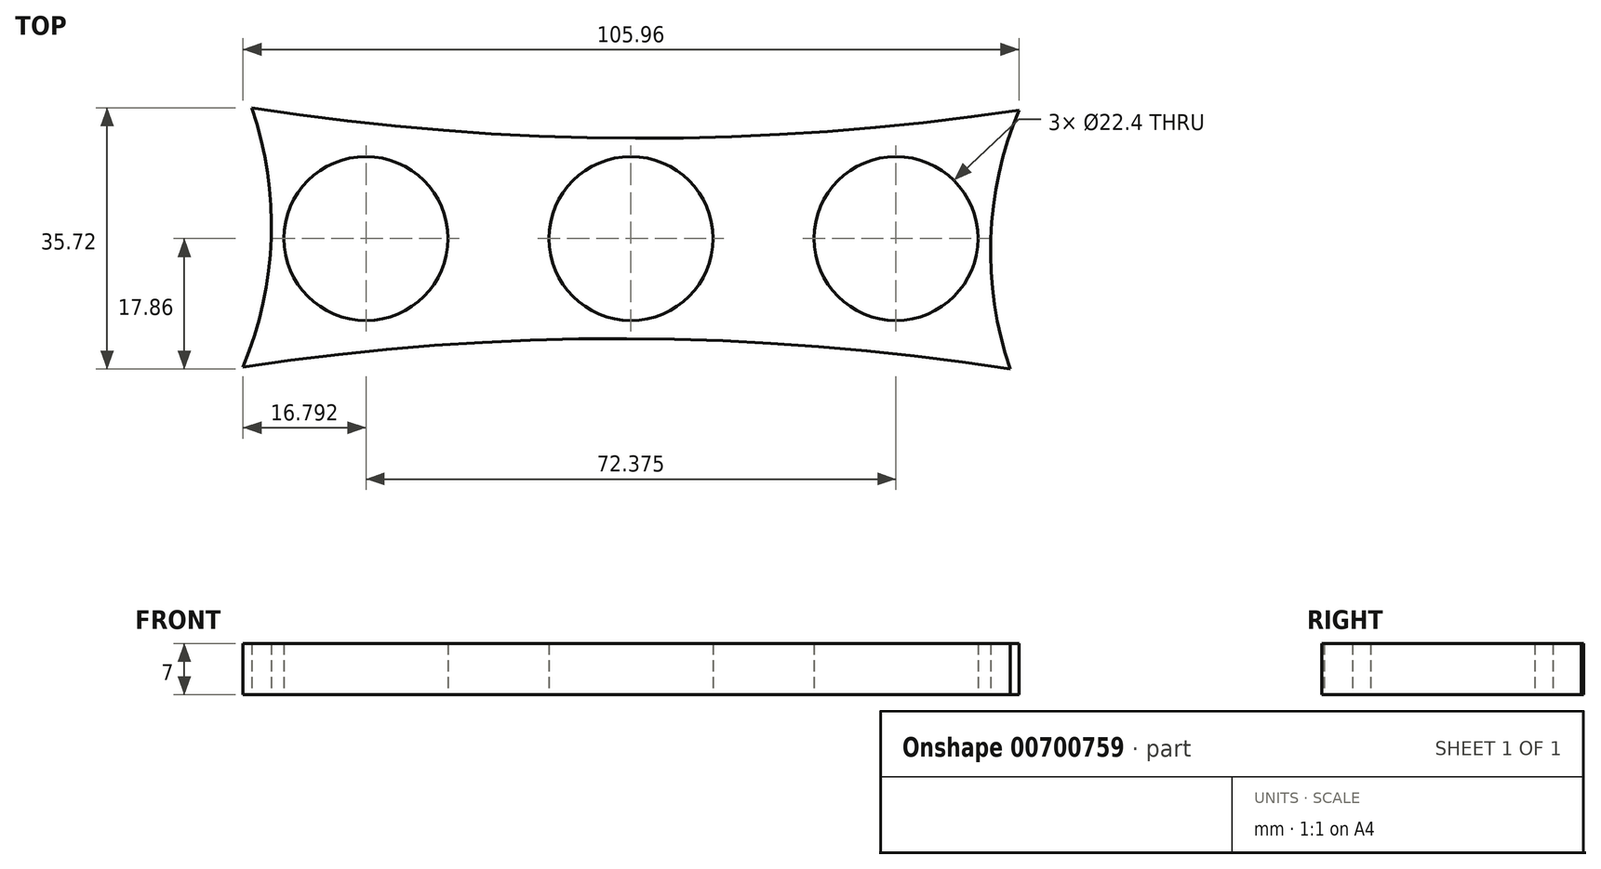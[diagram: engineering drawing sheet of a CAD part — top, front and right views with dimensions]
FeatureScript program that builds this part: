
annotation { "Feature Type Name" : "Feature", "Feature Type Description" : "" }
export const myFeature = defineFeature(function(context is Context, id is Id, definition is map)
    precondition{}
    {
        {
            var Q0;
            Q0=qCreatedBy(makeId("Top.planeOp"),FACE);
            var sketch = newSketch(context, id + "F0", { "sketchPlane" : qUnion([Q0])});
            skCircle(sketch, "E0", {"center": v(0, 0) * mm, "radius": 11.2 * mm});
            skCircle(sketch, "E1", {"center": v(-36.19, 0) * mm, "radius": 11.2 * mm});
            skArc(sketch, "E2", {"start": v(-49.1, 2.71) * mm, "mid": v(-49.38, 0.37) * mm, "end": v(-49.24, -1.98) * mm});
            skArc(sketch, "E3.1.0", {"start": v(49.1, -2.71) * mm, "mid": v(49.38, -0.37) * mm, "end": v(49.24, 1.98) * mm});
            skCircle(sketch, "E3.1.1", {"center": v(36.19, 0) * mm, "radius": 11.2 * mm});
            skArc(sketch, "E4", {"start": v(-49.37, -0.6) * mm, "mid": v(-49.26, 0.82) * mm, "end": v(-49.2, 2.24) * mm});
            skArc(sketch, "E5", {"start": v(-52.98, -17.56) * mm, "mid": v(-49.13, 0.04) * mm, "end": v(-51.76, 17.86) * mm});
            skArc(sketch, "E6.1.0", {"start": v(52.98, 17.56) * mm, "mid": v(49.13, -0.04) * mm, "end": v(51.76, -17.86) * mm});
            skArc(sketch, "E7", {"start": v(-51.76, 17.86) * mm, "mid": v(0.6, 13.7) * mm, "end": v(52.98, 17.56) * mm});
            skArc(sketch, "E8.1.0", {"start": v(51.76, -17.86) * mm, "mid": v(-0.6, -13.7) * mm, "end": v(-52.98, -17.56) * mm});
            skSolve(sketch);
        }
        {
            var Q0;
            Q0=makeQuery(id+"F0.imprint","IMPRINT",FACE,{"disambiguationData":[TD([[makeQuery(id+"F0.imprint","IMPRINT",EDGE,{"derivedFrom":sQuery(id+"F0.wireOp",EDGE,"E0")}),-1.0]])]});
            extrude(context, id + "F1", {"entities" : qUnion([Q0]), "depth" : 7 * mm, "offsetDistance" : 25 * mm});
        }
    });
